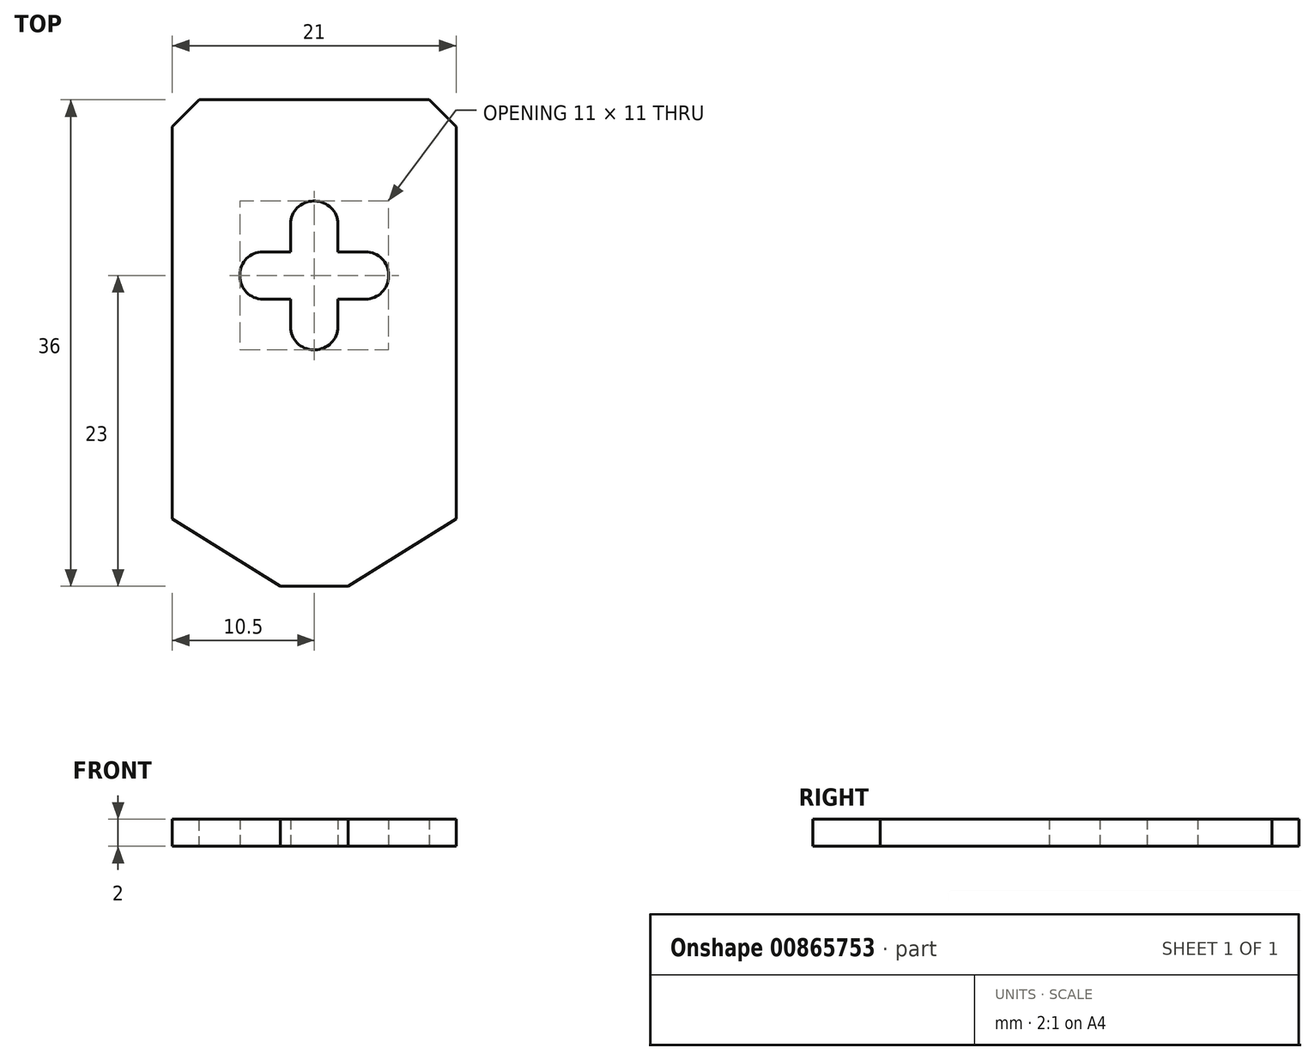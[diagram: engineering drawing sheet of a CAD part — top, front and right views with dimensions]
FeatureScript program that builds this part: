
annotation { "Feature Type Name" : "Feature", "Feature Type Description" : "" }
export const myFeature = defineFeature(function(context is Context, id is Id, definition is map)
    precondition{}
    {
        {
            var Q0;
            Q0=qCreatedBy(makeId("Top.planeOp"),FACE);
            var sketch = newSketch(context, id + "F0", { "sketchPlane" : qUnion([Q0])});
            skLineSegment(sketch, "E0.bottom", {"start": v(-10.5, -18) * mm, "end": v(10.5, -18) * mm});
            skLineSegment(sketch, "E0.top", {"start": v(-10.5, 18) * mm, "end": v(10.5, 18) * mm});
            skLineSegment(sketch, "E0.left", {"start": v(-10.5, -18) * mm, "end": v(-10.5, 18) * mm});
            skLineSegment(sketch, "E0.right", {"start": v(10.5, -18) * mm, "end": v(10.5, 18) * mm});
            skPoint(sketch, "E0.middle", {"position": v(0, 0) * mm});
            skLineSegment(sketch, "E1.bottom", {"start": v(1.75, -0.5) * mm, "end": v(-1.75, -0.5) * mm});
            skLineSegment(sketch, "E1.top", {"start": v(1.75, 10.5) * mm, "end": v(-1.75, 10.5) * mm});
            skLineSegment(sketch, "E1.left", {"start": v(1.75, -0.5) * mm, "end": v(1.75, 10.5) * mm});
            skLineSegment(sketch, "E1.right", {"start": v(-1.75, -0.5) * mm, "end": v(-1.75, 10.5) * mm});
            skPoint(sketch, "E1.middle", {"position": v(0, 5) * mm});
            skLineSegment(sketch, "E2.bottom", {"start": v(5.5, 3.25) * mm, "end": v(-5.5, 3.25) * mm});
            skLineSegment(sketch, "E2.top", {"start": v(5.5, 6.75) * mm, "end": v(-5.5, 6.75) * mm});
            skLineSegment(sketch, "E2.left", {"start": v(5.5, 3.25) * mm, "end": v(5.5, 6.75) * mm});
            skLineSegment(sketch, "E2.right", {"start": v(-5.5, 3.25) * mm, "end": v(-5.5, 6.75) * mm});
            skSolve(sketch);
        }
        {
            var Q0;
            Q0=makeQuery(id+"F0.imprint","IMPRINT",FACE,{"disambiguationData":[TD([[makeQuery(id+"F0.imprint","IMPRINT",EDGE,{"derivedFrom":sQuery(id+"F0.wireOp",EDGE,"E0.bottom")}),1.0]])]});
            extrude(context, id + "F1", {"entities" : qUnion([Q0]), "depth" : 2 * mm, "offsetDistance" : 25 * mm});
        }
        {
            var Q0;
            Q0=makeQuery(id+"F1.opExtrude","SWEPT_EDGE",EDGE,{"disambiguationData":[OSD([sQuery(id+"F0.wireOp",EDGE,"E0.top"),sQuery(id+"F0.wireOp",EDGE,"E0.right")])]});
            var Q1;
            Q1=makeQuery(id+"F1.opExtrude","SWEPT_EDGE",EDGE,{"disambiguationData":[OSD([sQuery(id+"F0.wireOp",EDGE,"E0.top"),sQuery(id+"F0.wireOp",EDGE,"E0.left")])]});
            chamfer(context, id + "F2", {"entities" : qUnion([Q0, Q1]), "width" : 2 * mm, "tangentPropagation" : true});
        }
        {
            var Q0;
            Q0=makeQuery(id+"F1.opExtrude","SWEPT_EDGE",EDGE,{"disambiguationData":[OSD([sQuery(id+"F0.wireOp",EDGE,"E0.bottom"),sQuery(id+"F0.wireOp",EDGE,"E0.right")])]});
            var Q1;
            Q1=makeQuery(id+"F1.opExtrude","SWEPT_EDGE",EDGE,{"disambiguationData":[OSD([sQuery(id+"F0.wireOp",EDGE,"E0.bottom"),sQuery(id+"F0.wireOp",EDGE,"E0.left")])]});
            chamfer(context, id + "F3", {"entities" : qUnion([Q0, Q1]), "chamferType" : ChamferType.TWO_OFFSETS, "width1" : 5 * mm, "oppositeDirection" : false, "width2" : 8 * mm, "tangentPropagation" : true});
        }
        {
            var Q0;
            Q0=makeQuery(id+"F1.opExtrude","SWEPT_EDGE",EDGE,{"disambiguationData":[OSD([sQuery(id+"F0.wireOp",EDGE,"E2.top"),sQuery(id+"F0.wireOp",EDGE,"E2.left")])]});
            var Q1;
            Q1=makeQuery(id+"F1.opExtrude","SWEPT_EDGE",EDGE,{"disambiguationData":[OSD([sQuery(id+"F0.wireOp",EDGE,"E1.top"),sQuery(id+"F0.wireOp",EDGE,"E1.left")])]});
            var Q2;
            Q2=makeQuery(id+"F1.opExtrude","SWEPT_EDGE",EDGE,{"disambiguationData":[OSD([sQuery(id+"F0.wireOp",EDGE,"E1.top"),sQuery(id+"F0.wireOp",EDGE,"E1.right")])]});
            var Q3;
            Q3=makeQuery(id+"F1.opExtrude","SWEPT_EDGE",EDGE,{"disambiguationData":[OSD([sQuery(id+"F0.wireOp",EDGE,"E2.top"),sQuery(id+"F0.wireOp",EDGE,"E2.right")])]});
            var Q4;
            Q4=makeQuery(id+"F1.opExtrude","SWEPT_EDGE",EDGE,{"disambiguationData":[OSD([sQuery(id+"F0.wireOp",EDGE,"E2.bottom"),sQuery(id+"F0.wireOp",EDGE,"E2.right")])]});
            var Q5;
            Q5=makeQuery(id+"F1.opExtrude","SWEPT_EDGE",EDGE,{"disambiguationData":[OSD([sQuery(id+"F0.wireOp",EDGE,"E1.bottom"),sQuery(id+"F0.wireOp",EDGE,"E1.right")])]});
            var Q6;
            Q6=makeQuery(id+"F1.opExtrude","SWEPT_EDGE",EDGE,{"disambiguationData":[OSD([sQuery(id+"F0.wireOp",EDGE,"E1.bottom"),sQuery(id+"F0.wireOp",EDGE,"E1.left")])]});
            var Q7;
            Q7=makeQuery(id+"F1.opExtrude","SWEPT_EDGE",EDGE,{"disambiguationData":[OSD([sQuery(id+"F0.wireOp",EDGE,"E2.bottom"),sQuery(id+"F0.wireOp",EDGE,"E2.left")])]});
            fillet(context, id + "F4", {"entities" : qUnion([Q0, Q1, Q2, Q3, Q4, Q5, Q6, Q7]), "radius" : 1.7 * mm, "tangentPropagation" : true, "allowEdgeOverflow" : false});
        }
    });
